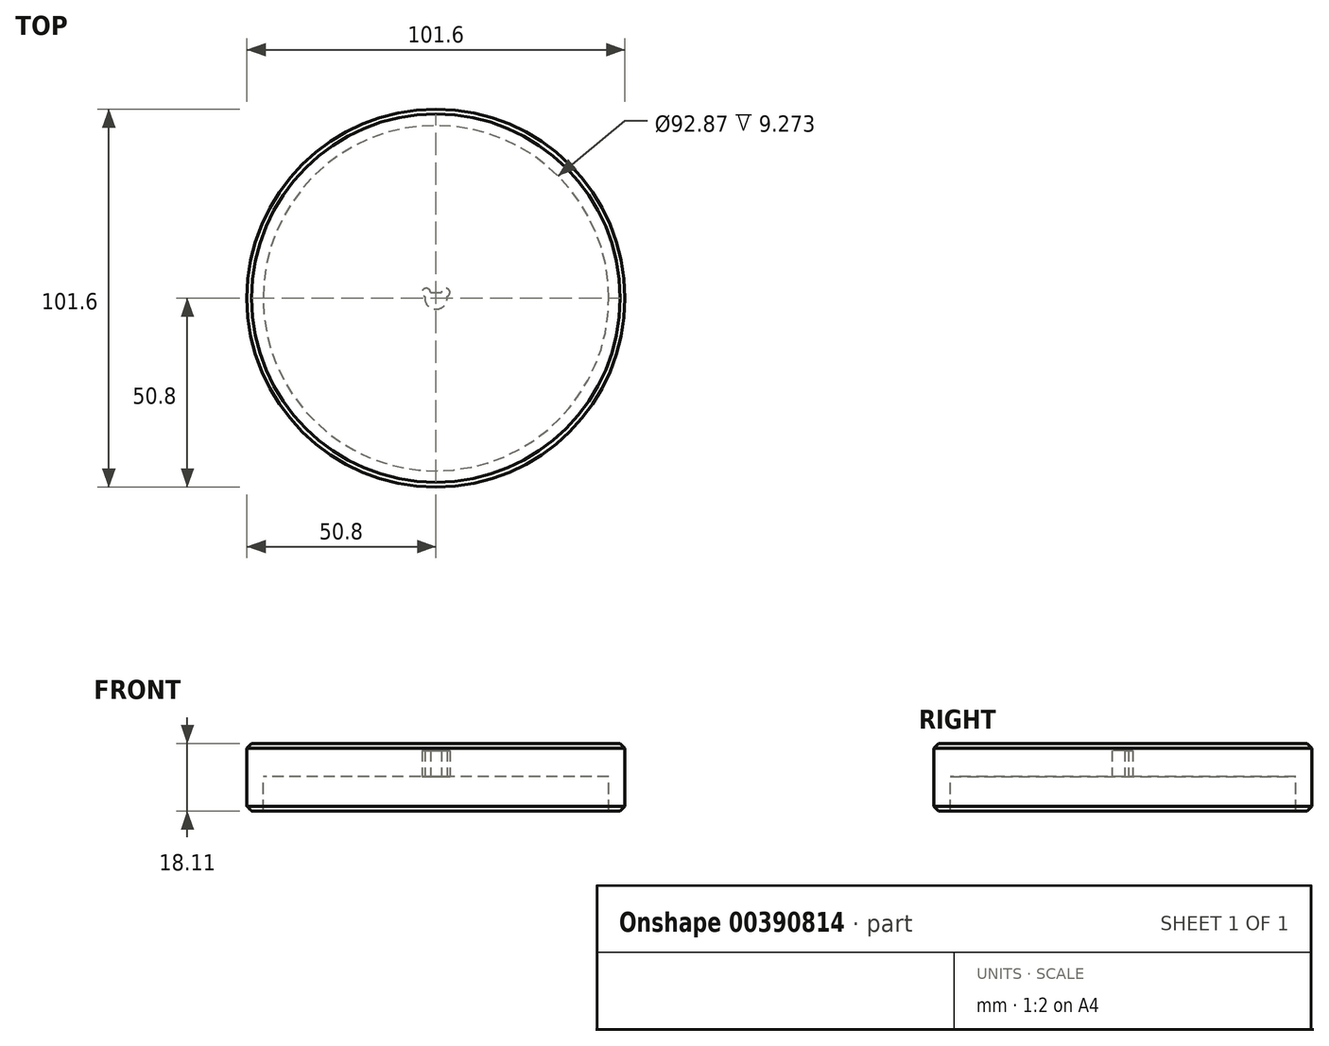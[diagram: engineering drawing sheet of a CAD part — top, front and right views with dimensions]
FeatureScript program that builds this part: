
annotation { "Feature Type Name" : "Feature", "Feature Type Description" : "" }
export const myFeature = defineFeature(function(context is Context, id is Id, definition is map)
    precondition{}
    {
        {
            var Q0;
            Q0=qCreatedBy(makeId("Front.planeOp"),FACE);
            var sketch = newSketch(context, id + "F0", { "sketchPlane" : qUnion([Q0])});
            skLineSegment(sketch, "E0", {"start": v(0, 3.1) * mm, "end": v(-50.8, 3.1) * mm});
            skLineSegment(sketch, "E1", {"start": v(-50.8, 3.1) * mm, "end": v(-50.8, -15) * mm});
            skLineSegment(sketch, "E2", {"start": v(-50.8, -15) * mm, "end": v(-46.44, -15) * mm});
            skLineSegment(sketch, "E3", {"start": v(-1, -5.73) * mm, "end": v(-1, 0) * mm});
            skLineSegment(sketch, "E4", {"start": v(-1, 0) * mm, "end": v(0, 0) * mm});
            skLineSegment(sketch, "E5", {"start": v(0, 3.1) * mm, "end": v(0, 0) * mm});
            skLineSegment(sketch, "E6", {"start": v(0, 34.35) * mm, "end": v(0, -25.56) * mm, "construction": true});
            skLineSegment(sketch, "E7", {"start": v(-1, -5.73) * mm, "end": v(-46.44, -5.73) * mm});
            skLineSegment(sketch, "E8", {"start": v(-46.44, -5.73) * mm, "end": v(-46.44, -15) * mm});
            skSolve(sketch);
        }
        {
            var Q0;
            Q0=makeQuery(id+"F0.imprint","IMPRINT",FACE,{"disambiguationData":[TD([[makeQuery(id+"F0.imprint","IMPRINT",EDGE,{"derivedFrom":sQuery(id+"F0.wireOp",EDGE,"E0")}),1.0]])]});
            var Q1;
            Q1=sQuery(id+"F0.wireOp",EDGE,"E1");
            var Q2;
            Q2=sQuery(id+"F0.wireOp",EDGE,"E3");
            var Q3;
            Q3=sQuery(id+"F0.wireOp",EDGE,"E4");
            var Q4;
            Q4=sQuery(id+"F0.wireOp",EDGE,"E0");
            var Q5;
            Q5=sQuery(id+"F0.wireOp",EDGE,"E2");
            var Q6;
            Q6=sQuery(id+"F0.wireOp",EDGE,"E6");
            revolve(context, id + "F1", {"entities" : qUnion([Q0]), "surfaceEntities" : qUnion([Q1, Q2, Q3, Q4, Q5]), "axis" : qUnion([Q6]), "revolveType" : RevolveType.FULL});
        }
        {
            var Q0;
            Q0=makeQuery(id+"F1.opRevolve","SWEPT_EDGE",EDGE,{"disambiguationData":[OSD([sQuery(id+"F0.wireOp",VERTEX,"E0.end")])]});
            var Q1;
            Q1=makeQuery(id+"F1.opRevolve","SWEPT_EDGE",EDGE,{"disambiguationData":[OSD([sQuery(id+"F0.wireOp",EDGE,"E0"),sQuery(id+"F0.wireOp",EDGE,"E1")])]});
            chamfer(context, id + "F2", {"entities" : qUnion([Q0, Q1]), "width" : 1.27 * mm, "tangentPropagation" : true});
        }
        {
            var Q0;
            Q0=makeQuery(id+"F1.opRevolve","SWEPT_FACE",FACE,{"disambiguationData":[OSD([sQuery(id+"F0.wireOp",EDGE,"E7")])]});
            var sketch = newSketch(context, id + "F3", { "sketchPlane" : qUnion([Q0])});
            skLineSegment(sketch, "E9", {"start": v(-1.46, -1.5) * mm, "end": v(1.46, -1.5) * mm});
            skArc(sketch, "E10", {"start": v(2.97, -0.42) * mm, "mid": v(0, 3) * mm, "end": v(-2.97, -0.42) * mm});
            skArc(sketch, "E11", {"start": v(-2.97, -0.42) * mm, "mid": v(-3.26, -2.43) * mm, "end": v(-1.46, -1.5) * mm});
            skArc(sketch, "E12", {"start": v(1.46, -1.5) * mm, "mid": v(3.26, -2.43) * mm, "end": v(2.97, -0.42) * mm});
            skSolve(sketch);
        }
        {
            var Q0;
            Q0 = qSketchRegion(id + "F3", true);
            extrude(context, id + "F4", {"entities" : qUnion([Q0]), "operationType" : NewBodyOperationType.REMOVE, "oppositeDirection" : true, "depth" : 7 * mm});
        }
        {
            var Q0;
            Q0=makeQuery(id+"F1.opRevolve","SWEPT_EDGE",EDGE,{"disambiguationData":[OSD([sQuery(id+"F0.wireOp",EDGE,"E1"),sQuery(id+"F0.wireOp",EDGE,"E2")])]});
            chamfer(context, id + "F5", {"entities" : qUnion([Q0]), "width" : 1.27 * mm, "tangentPropagation" : true});
        }
    });
